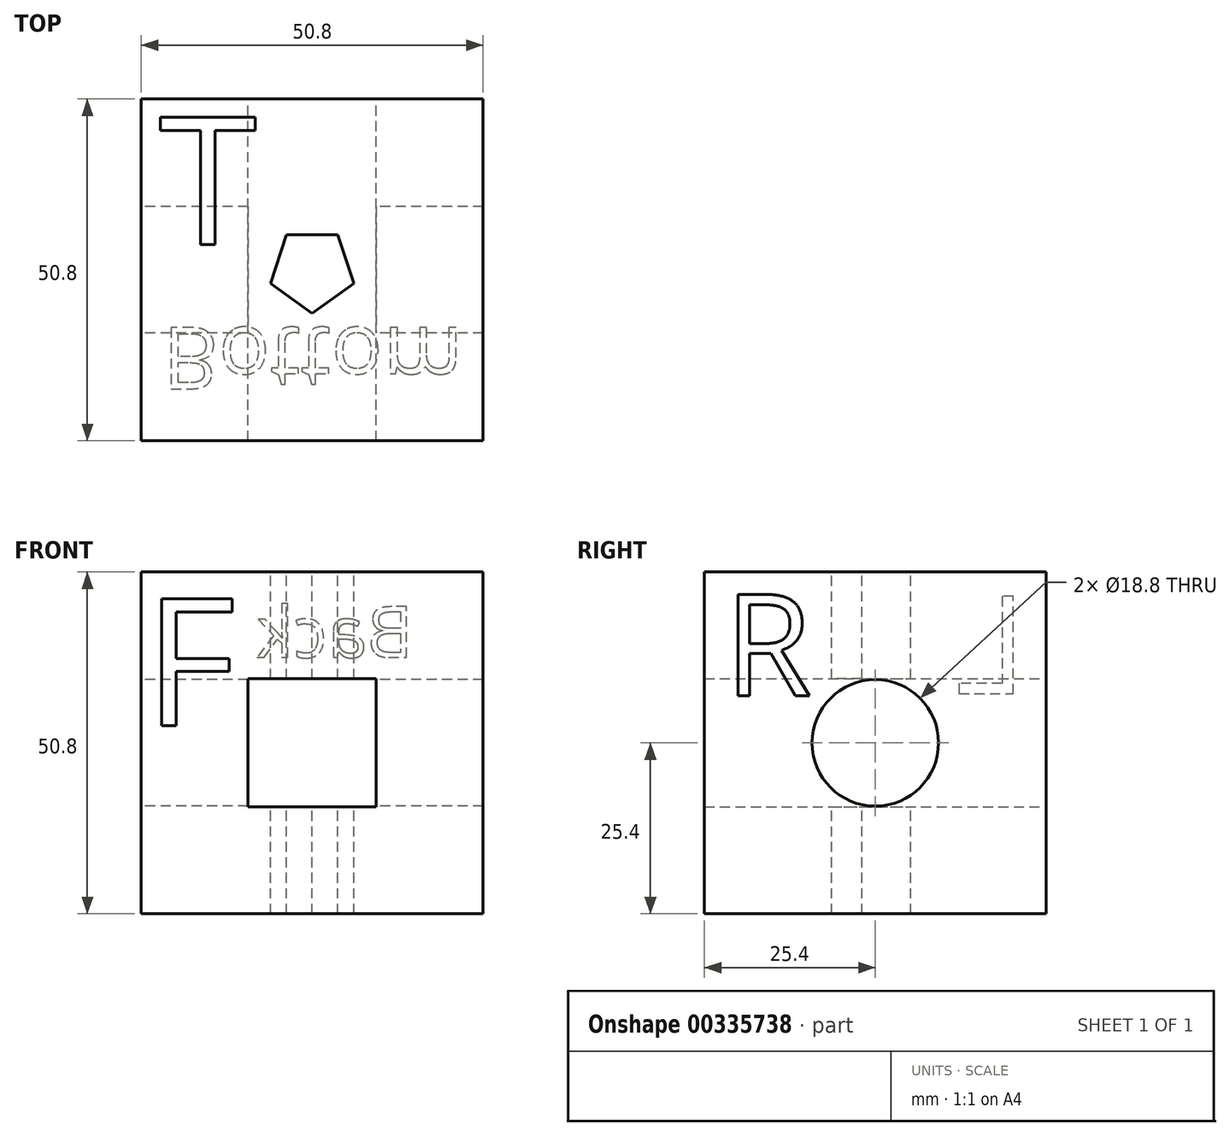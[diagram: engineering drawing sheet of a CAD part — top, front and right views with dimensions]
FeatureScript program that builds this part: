
annotation { "Feature Type Name" : "Feature", "Feature Type Description" : "" }
export const myFeature = defineFeature(function(context is Context, id is Id, definition is map)
    precondition{}
    {
        {
            var Q0;
            Q0=qCreatedBy(makeId("Front.planeOp"),FACE);
            var sketch = newSketch(context, id + "F0", { "sketchPlane" : qUnion([Q0])});
            skLineSegment(sketch, "E0.bottom", {"start": v(25.4, 25.4) * mm, "end": v(-25.4, 25.4) * mm});
            skLineSegment(sketch, "E0.top", {"start": v(25.4, -25.4) * mm, "end": v(-25.4, -25.4) * mm});
            skLineSegment(sketch, "E0.left", {"start": v(25.4, 25.4) * mm, "end": v(25.4, -25.4) * mm});
            skLineSegment(sketch, "E0.right", {"start": v(-25.4, 25.4) * mm, "end": v(-25.4, -25.4) * mm});
            skPoint(sketch, "E0.middle", {"position": v(0, 0) * mm});
            skLineSegment(sketch, "E1.bottom", {"start": v(9.52, 9.52) * mm, "end": v(-9.53, 9.52) * mm});
            skLineSegment(sketch, "E1.top", {"start": v(9.52, -9.52) * mm, "end": v(-9.53, -9.52) * mm});
            skLineSegment(sketch, "E1.left", {"start": v(9.52, 9.52) * mm, "end": v(9.52, -9.52) * mm});
            skLineSegment(sketch, "E1.right", {"start": v(-9.53, 9.52) * mm, "end": v(-9.53, -9.52) * mm});
            skSolve(sketch);
        }
        {
            var Q0;
            Q0=makeQuery(id+"F0.imprint","IMPRINT",FACE,{"disambiguationData":[TD([[makeQuery(id+"F0.imprint","IMPRINT",EDGE,{"derivedFrom":sQuery(id+"F0.wireOp",EDGE,"E0.bottom")}),1.0]])]});
            extrude(context, id + "F1", {"entities" : qUnion([Q0]), "depth" : 50.8 * mm, "symmetric" : true});
        }
        {
            var Q0;
            Q0=qCreatedBy(makeId("Right.planeOp"),FACE);
            var sketch = newSketch(context, id + "F2", { "sketchPlane" : qUnion([Q0])});
            skCircle(sketch, "E2", {"center": v(0, 0) * mm, "radius": 9.4 * mm});
            skSolve(sketch);
        }
        {
            var Q0;
            Q0 = qSketchRegion(id + "F2", true);
            extrude(context, id + "F3", {"entities" : qUnion([Q0]), "operationType" : NewBodyOperationType.REMOVE, "depth" : 76.2 * mm, "symmetric" : true});
        }
        {
            var Q0;
            Q0=qCreatedBy(makeId("Top.planeOp"),FACE);
            var sketch = newSketch(context, id + "F4", { "sketchPlane" : qUnion([Q0])});
            skCircle(sketch, "E3.cCircle", {"center": v(0, 0) * mm, "radius": 5.24 * mm, "construction": true});
            skLineSegment(sketch, "E3.0", {"start": v(-3.8, 5.24) * mm, "end": v(3.8, 5.24) * mm});
            skLineSegment(sketch, "E3.1", {"start": v(3.8, 5.24) * mm, "end": v(6.16, -2) * mm});
            skLineSegment(sketch, "E3.2", {"start": v(6.16, -2) * mm, "end": v(0, -6.48) * mm});
            skLineSegment(sketch, "E3.3", {"start": v(0, -6.48) * mm, "end": v(-6.16, -2) * mm});
            skLineSegment(sketch, "E3.4", {"start": v(-6.16, -2) * mm, "end": v(-3.81, 5.24) * mm});
            skPoint(sketch, "E3.0.midPoint", {"position": v(0, 5.24) * mm});
            skSolve(sketch);
        }
        {
            var Q0;
            Q0 = qSketchRegion(id + "F4", true);
            extrude(context, id + "F5", {"entities" : qUnion([Q0]), "operationType" : NewBodyOperationType.REMOVE, "oppositeDirection" : true, "depth" : 76.2 * mm, "symmetric" : true});
        }
        {
            var Q0;
            Q0=makeQuery(id+"F1.opExtrude","CAP_FACE",FACE,{"disambiguationData":[OSD([sQuery(id+"F0.wireOp",EDGE,"E0.bottom"),sQuery(id+"F0.wireOp",EDGE,"E0.top"),sQuery(id+"F0.wireOp",EDGE,"E0.left"),sQuery(id+"F0.wireOp",EDGE,"E0.right"),sQuery(id+"F0.wireOp",EDGE,"E1.bottom"),sQuery(id+"F0.wireOp",EDGE,"E1.top"),sQuery(id+"F0.wireOp",EDGE,"E1.left"),sQuery(id+"F0.wireOp",EDGE,"E1.right")])],"isStart":false});
            var sketch = newSketch(context, id + "F6", { "sketchPlane" : qUnion([Q0])});
            skText(sketch, "E4", { "text": "F", "fontName": "OpenSans-Regular.ttf"});
            const initialGuessF6  = {"E4": [-0.025, 0.00254, 1, 0, 0.01905]};
            skSetInitialGuess(sketch, initialGuessF6);
            skSolve(sketch);
        }
        {
            var Q0;
            Q0 = qSketchRegion(id + "F6", true);
            extrude(context, id + "F7", {"entities" : qUnion([Q0]), "operationType" : NewBodyOperationType.REMOVE, "oppositeDirection" : true, "depth" : 0.03 * mm});
        }
        {
            var Q0;
            Q0=makeQuery(id+"F1.opExtrude","SWEPT_FACE",FACE,{"disambiguationData":[OSD([sQuery(id+"F0.wireOp",EDGE,"E0.bottom")])]});
            var sketch = newSketch(context, id + "F8", { "sketchPlane" : qUnion([Q0])});
            skText(sketch, "E5", { "text": "T", "fontName": "OpenSans-Regular.ttf"});
            const initialGuessF8  = {"E5": [-0.02283, 0.00378, 1, 0, 0.01905]};
            skSetInitialGuess(sketch, initialGuessF8);
            skSolve(sketch);
        }
        {
            var Q0;
            Q0 = qSketchRegion(id + "F8", true);
            extrude(context, id + "F9", {"entities" : qUnion([Q0]), "operationType" : NewBodyOperationType.REMOVE, "oppositeDirection" : true, "depth" : 0.03 * mm});
        }
        {
            var Q0;
            Q0=makeQuery(id+"F1.opExtrude","CAP_FACE",FACE,{"disambiguationData":[OSD([sQuery(id+"F0.wireOp",EDGE,"E0.bottom"),sQuery(id+"F0.wireOp",EDGE,"E0.top"),sQuery(id+"F0.wireOp",EDGE,"E0.left"),sQuery(id+"F0.wireOp",EDGE,"E0.right"),sQuery(id+"F0.wireOp",EDGE,"E1.bottom"),sQuery(id+"F0.wireOp",EDGE,"E1.top"),sQuery(id+"F0.wireOp",EDGE,"E1.left"),sQuery(id+"F0.wireOp",EDGE,"E1.right")])],"isStart":true});
            var sketch = newSketch(context, id + "F10", { "sketchPlane" : qUnion([Q0])});
            skText(sketch, "E6", { "text": "Back", "fontName": "OpenSans-Regular.ttf"});
            const initialGuessF10  = {"E6": [-0.01502, 0.0127, 1, 0, 0.00762]};
            skSetInitialGuess(sketch, initialGuessF10);
            skSolve(sketch);
        }
        {
            var Q0;
            Q0 = qSketchRegion(id + "F10", true);
            extrude(context, id + "F11", {"entities" : qUnion([Q0]), "operationType" : NewBodyOperationType.REMOVE, "oppositeDirection" : true, "depth" : 0.03 * mm});
        }
        {
            var Q0;
            Q0=makeQuery(id+"F1.opExtrude","SWEPT_FACE",FACE,{"disambiguationData":[OSD([sQuery(id+"F0.wireOp",EDGE,"E0.top")])]});
            var sketch = newSketch(context, id + "F12", { "sketchPlane" : qUnion([Q0])});
            skText(sketch, "E7", { "text": "Bottom", "fontName": "OpenSans-Regular.ttf"});
            const initialGuessF12  = {"E7": [-0.02223, 0.00857, 1, 0, 0.0092]};
            skSetInitialGuess(sketch, initialGuessF12);
            skSolve(sketch);
        }
        {
            var Q0;
            Q0 = qSketchRegion(id + "F12", true);
            extrude(context, id + "F13", {"entities" : qUnion([Q0]), "operationType" : NewBodyOperationType.REMOVE, "oppositeDirection" : true, "depth" : 0.03 * mm});
        }
        {
            var Q0;
            Q0=makeQuery(id+"F1.opExtrude","SWEPT_FACE",FACE,{"disambiguationData":[OSD([sQuery(id+"F0.wireOp",EDGE,"E0.right")])]});
            var sketch = newSketch(context, id + "F14", { "sketchPlane" : qUnion([Q0])});
            skText(sketch, "E8", { "text": "L", "fontName": "OpenSans-Regular.ttf"});
            const initialGuessF14  = {"E8": [-0.0225, 0.0073, 1, 0, 0.0146]};
            skSetInitialGuess(sketch, initialGuessF14);
            skSolve(sketch);
        }
        {
            var Q0;
            Q0 = qSketchRegion(id + "F14", true);
            extrude(context, id + "F15", {"entities" : qUnion([Q0]), "operationType" : NewBodyOperationType.REMOVE, "oppositeDirection" : true, "depth" : 0.03 * mm});
        }
        {
            var Q0;
            Q0=makeQuery(id+"F1.opExtrude","SWEPT_FACE",FACE,{"disambiguationData":[OSD([sQuery(id+"F0.wireOp",EDGE,"E0.left")])]});
            var sketch = newSketch(context, id + "F16", { "sketchPlane" : qUnion([Q0])});
            skText(sketch, "E9", { "text": "R", "fontName": "OpenSans-Regular.ttf"});
            const initialGuessF16  = {"E9": [-0.0225, 0.007, 1, 0, 0.0152]};
            skSetInitialGuess(sketch, initialGuessF16);
            skSolve(sketch);
        }
        {
            var Q0;
            Q0 = qSketchRegion(id + "F16", true);
            extrude(context, id + "F17", {"entities" : qUnion([Q0]), "operationType" : NewBodyOperationType.REMOVE, "oppositeDirection" : true, "depth" : 0.03 * mm});
        }
    });
